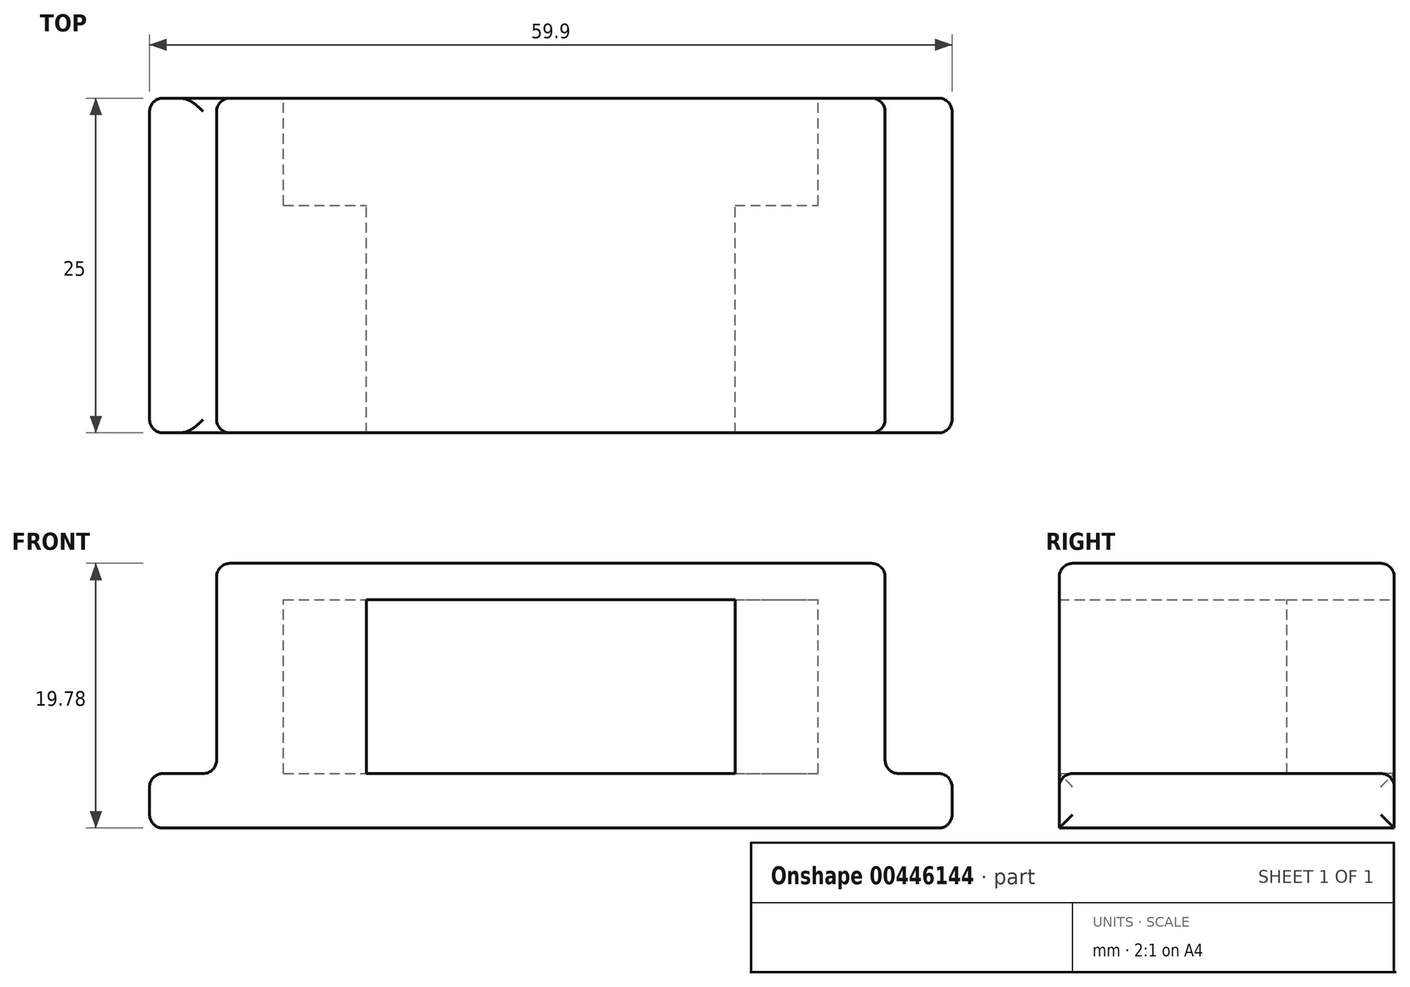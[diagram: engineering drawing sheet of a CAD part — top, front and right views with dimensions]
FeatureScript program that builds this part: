
annotation { "Feature Type Name" : "Feature", "Feature Type Description" : "" }
export const myFeature = defineFeature(function(context is Context, id is Id, definition is map)
    precondition{}
    {
        {
            var Q0;
            Q0=qCreatedBy(makeId("Front.planeOp"),FACE);
            var sketch = newSketch(context, id + "F0", { "sketchPlane" : qUnion([Q0])});
            skLineSegment(sketch, "E0.bottom", {"start": v(0, 0) * mm, "end": v(27.5, 0) * mm});
            skLineSegment(sketch, "E0.top", {"start": v(0, 13) * mm, "end": v(27.5, 13) * mm});
            skLineSegment(sketch, "E0.left", {"start": v(0, 0) * mm, "end": v(0, 13) * mm});
            skLineSegment(sketch, "E0.right", {"start": v(27.5, 0) * mm, "end": v(27.5, 13) * mm});
            skPoint(sketch, "E1.oppositeSnap0", {"position": v(13.75, 13) * mm});
            skLineSegment(sketch, "E1.bottom", {"start": v(-6.2, 0) * mm, "end": v(33.7, 0) * mm});
            skLineSegment(sketch, "E1.top", {"start": v(-6.2, 13) * mm, "end": v(33.7, 13) * mm});
            skLineSegment(sketch, "E1.left", {"start": v(-6.2, 0) * mm, "end": v(-6.2, 13) * mm});
            skLineSegment(sketch, "E1.right", {"start": v(33.7, 0) * mm, "end": v(33.7, 13) * mm});
            skLineSegment(sketch, "E2.bottom", {"start": v(-11.2, 15.7) * mm, "end": v(38.7, 15.7) * mm});
            skLineSegment(sketch, "E2.top", {"start": v(-11.2, -4.07) * mm, "end": v(38.7, -4.07) * mm});
            skLineSegment(sketch, "E2.left", {"start": v(-11.2, 15.7) * mm, "end": v(-11.2, -4.07) * mm});
            skLineSegment(sketch, "E2.right", {"start": v(38.7, 15.7) * mm, "end": v(38.7, -4.07) * mm});
            skLineSegment(sketch, "E3", {"start": v(-11.2, 0) * mm, "end": v(-16.2, 0) * mm});
            skLineSegment(sketch, "E4", {"start": v(-16.2, 0) * mm, "end": v(-16.2, -4.07) * mm});
            skLineSegment(sketch, "E5", {"start": v(-16.2, -4.07) * mm, "end": v(-11.2, -4.07) * mm});
            skLineSegment(sketch, "E6", {"start": v(38.7, 0) * mm, "end": v(43.7, 0) * mm});
            skLineSegment(sketch, "E7", {"start": v(43.7, 0) * mm, "end": v(43.7, -4.07) * mm});
            skLineSegment(sketch, "E8", {"start": v(43.7, -4.07) * mm, "end": v(38.7, -4.07) * mm});
            skSolve(sketch);
        }
        {
            var Q0;
            {var subQ2=sQuery(id+"F0.wireOp",EDGE,"E3");Q0=makeQuery(id+"F0.imprint","IMPRINT",FACE,{"disambiguationData":[TD([[makeQuery(id+"F0.imprint","IMPRINT",EDGE,{"derivedFrom":subQ2}),1.0]])]});}
            var Q1;
            {var subQ3=sQuery(id+"F0.wireOp",EDGE,"E1.left");Q1=makeQuery(id+"F0.imprint","IMPRINT",FACE,{"disambiguationData":[TD([[makeQuery(id+"F0.imprint","IMPRINT",EDGE,{"derivedFrom":subQ3}),1.0]])]});}
            var Q2;
            {var subQ2=sQuery(id+"F0.wireOp",EDGE,"E6");Q2=makeQuery(id+"F0.imprint","IMPRINT",FACE,{"disambiguationData":[TD([[makeQuery(id+"F0.imprint","IMPRINT",EDGE,{"derivedFrom":subQ2}),-1.0]])]});}
            var Q3;
            {var subQ0=sQuery(id+"F0.wireOp",EDGE,"E0.left");Q3=makeQuery(id+"F0.imprint","IMPRINT",FACE,{"disambiguationData":[TD([[makeQuery(id+"F0.imprint","IMPRINT",EDGE,{"derivedFrom":subQ0}),1.0]])]});}
            var Q4;
            {var subQ0=sQuery(id+"F0.wireOp",EDGE,"E0.right");Q4=makeQuery(id+"F0.imprint","IMPRINT",FACE,{"disambiguationData":[TD([[makeQuery(id+"F0.imprint","IMPRINT",EDGE,{"derivedFrom":subQ0}),-1.0]])]});}
            extrude(context, id + "F1", {"entities" : qUnion([Q0, Q1, Q2, Q3, Q4]), "depth" : 25 * mm});
        }
        {
            var Q0;
            {var subQ0=sQuery(id+"F0.wireOp",EDGE,"E0.right");Q0=makeQuery(id+"F0.imprint","IMPRINT",FACE,{"disambiguationData":[TD([[makeQuery(id+"F0.imprint","IMPRINT",EDGE,{"derivedFrom":subQ0}),-1.0]])]});}
            var Q1;
            {var subQ0=sQuery(id+"F0.wireOp",EDGE,"E0.left");Q1=makeQuery(id+"F0.imprint","IMPRINT",FACE,{"disambiguationData":[TD([[makeQuery(id+"F0.imprint","IMPRINT",EDGE,{"derivedFrom":subQ0}),1.0]])]});}
            extrude(context, id + "F2", {"entities" : qUnion([Q0, Q1]), "operationType" : NewBodyOperationType.REMOVE, "depth" : 8 * mm});
        }
        {
            var Q0;
            Q0=makeQuery(id+"F1.opExtrude","SWEPT_FACE",FACE,{"disambiguationData":[OSD([sQuery(id+"F0.wireOp",EDGE,"E2.bottom")])]});
            var Q1;
            Q1=makeQuery(id+"F1.opExtrude","SWEPT_FACE",FACE,{"disambiguationData":[OSD([sQuery(id+"F0.wireOp",EDGE,"E2.right")])]});
            var Q2;
            Q2=makeQuery(id+"F1.opExtrude","SWEPT_FACE",FACE,{"disambiguationData":[OSD([sQuery(id+"F0.wireOp",EDGE,"E6")])]});
            var Q3;
            Q3=makeQuery(id+"F1.opExtrude","SWEPT_FACE",FACE,{"disambiguationData":[OSD([sQuery(id+"F0.wireOp",EDGE,"E7")])]});
            var Q4;
            Q4=makeQuery(id+"F1.opExtrude","SWEPT_FACE",FACE,{"disambiguationData":[OSD([sQuery(id+"F0.wireOp",EDGE,"E2.left")])]});
            var Q5;
            Q5=makeQuery(id+"F1.opExtrude","SWEPT_EDGE",EDGE,{"disambiguationData":[OSD([sQuery(id+"F0.wireOp",EDGE,"E3"),sQuery(id+"F0.wireOp",EDGE,"E4")])]});
            var Q6;
            Q6=makeQuery(id+"F1.opExtrude","SWEPT_FACE",FACE,{"disambiguationData":[OSD([sQuery(id+"F0.wireOp",EDGE,"E4")])]});
            fillet(context, id + "F3", {"entities" : qUnion([Q0, Q1, Q2, Q3, Q4, Q5, Q6]), "radius" : 1 * mm, "tangentPropagation" : true, "allowEdgeOverflow" : false});
        }
    });
